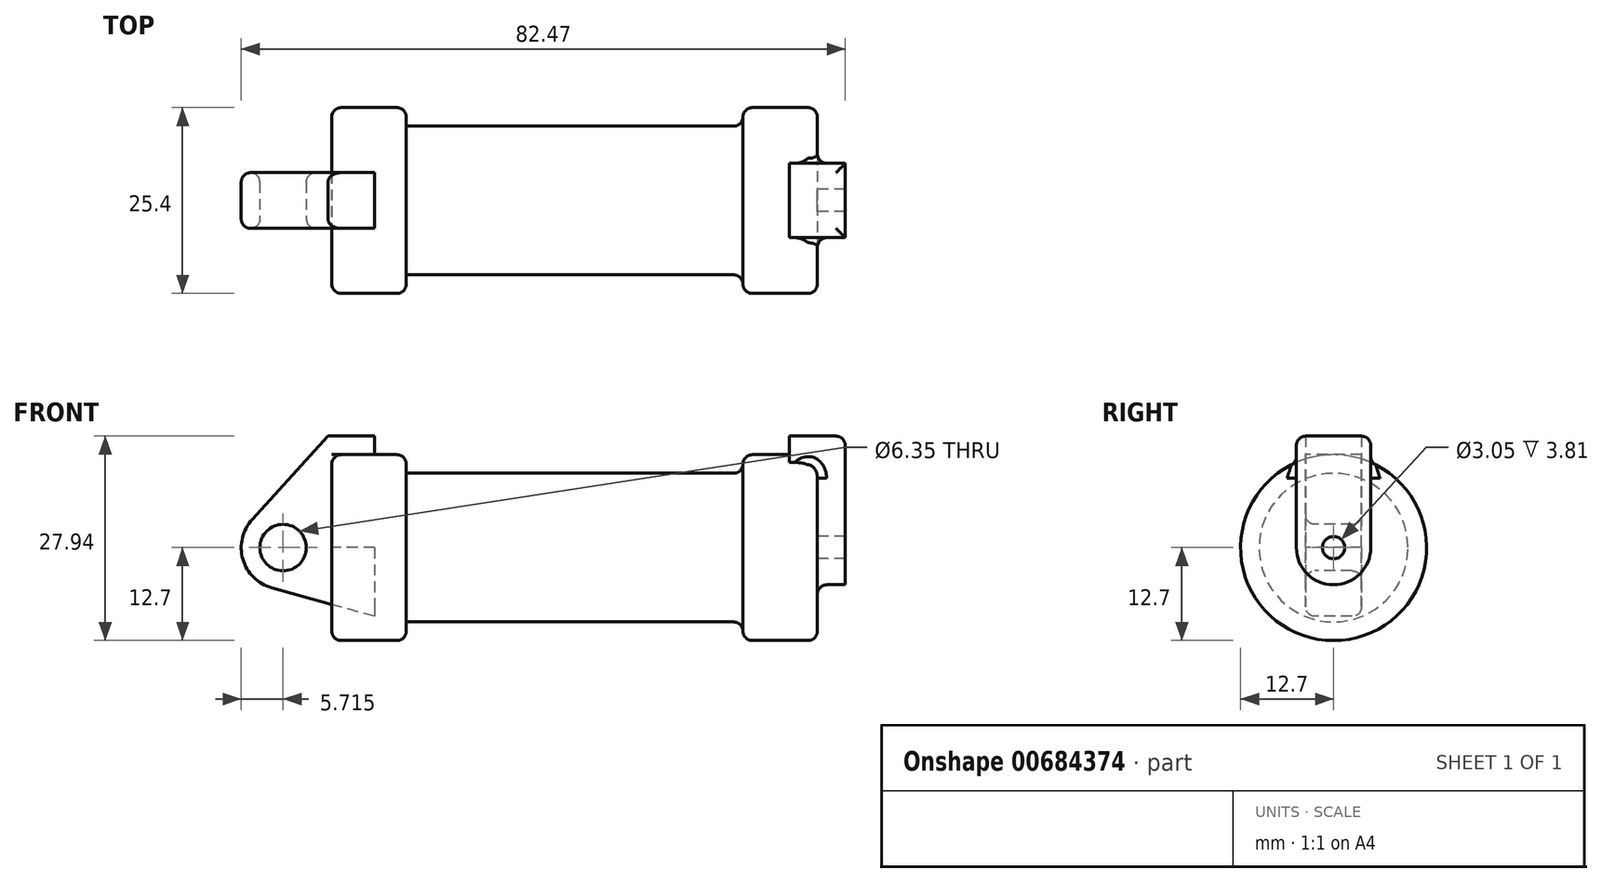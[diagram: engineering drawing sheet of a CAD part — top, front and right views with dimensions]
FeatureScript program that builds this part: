
annotation { "Feature Type Name" : "Feature", "Feature Type Description" : "" }
export const myFeature = defineFeature(function(context is Context, id is Id, definition is map)
    precondition{}
    {
        {
            var Q0;
            Q0=qCreatedBy(makeId("Front.planeOp"),FACE);
            var sketch = newSketch(context, id + "F0", { "sketchPlane" : qUnion([Q0])});
            skLineSegment(sketch, "E0", {"start": v(0, 0) * mm, "end": v(0, 12.7) * mm});
            skLineSegment(sketch, "E1", {"start": v(0, 12.7) * mm, "end": v(10.16, 12.7) * mm});
            skLineSegment(sketch, "E2", {"start": v(10.16, 12.7) * mm, "end": v(10.16, 10.16) * mm});
            skLineSegment(sketch, "E3", {"start": v(10.16, 10.16) * mm, "end": v(56.13, 10.16) * mm});
            skLineSegment(sketch, "E4", {"start": v(56.13, 10.16) * mm, "end": v(56.13, 12.7) * mm});
            skLineSegment(sketch, "E5", {"start": v(56.13, 12.7) * mm, "end": v(66.3, 12.7) * mm});
            skLineSegment(sketch, "E6", {"start": v(66.3, 12.7) * mm, "end": v(66.3, 0) * mm});
            skLineSegment(sketch, "E7", {"start": v(66.3, 0) * mm, "end": v(0, 0) * mm});
            skLineSegment(sketch, "E8", {"start": v(5.84, 15.24) * mm, "end": v(-0.5, 15.24) * mm});
            skLineSegment(sketch, "E9", {"start": v(-0.5, 15.24) * mm, "end": v(-10.88, 3.85) * mm});
            skLineSegment(sketch, "E10", {"start": v(0, 0) * mm, "end": v(-6.65, 0) * mm});
            skCircle(sketch, "E11", {"center": v(-6.65, 0) * mm, "radius": 5.72 * mm});
            skCircle(sketch, "E12", {"center": v(-6.65, 0) * mm, "radius": 3.18 * mm});
            skLineSegment(sketch, "E13", {"start": v(5.84, 15.24) * mm, "end": v(5.84, -9.4) * mm});
            skLineSegment(sketch, "E14", {"start": v(5.84, -9.4) * mm, "end": v(-8.18, -5.5) * mm});
            skSolve(sketch);
        }
        {
            var Q0;
            {var subQ0=sQuery(id+"F0.wireOp",EDGE,"E0");Q0=makeQuery(id+"F0.imprint","IMPRINT",FACE,{"disambiguationData":[TD([[makeQuery(id+"F0.imprint","IMPRINT",EDGE,{"derivedFrom":subQ0}),-1.0]])]});}
            var Q1;
            {var subQ0=sQuery(id+"F0.wireOp",EDGE,"E2");Q1=makeQuery(id+"F0.imprint","IMPRINT",FACE,{"disambiguationData":[TD([[makeQuery(id+"F0.imprint","IMPRINT",EDGE,{"derivedFrom":subQ0}),-1.0]])]});}
            var Q2;
            Q2=sQuery(id+"F0.wireOp",EDGE,"E7");
            var Q3;
            Q3=sQuery(id+"F0.wireOp",EDGE,"E7");
            revolve(context, id + "F1", {"entities" : qUnion([Q0, Q1]), "surfaceEntities" : qUnion([Q2]), "axis" : qUnion([Q3]), "revolveType" : RevolveType.FULL});
        }
        {
            var Q0;
            Q0=makeQuery(id+"F1.opRevolve","SWEPT_FACE",FACE,{"disambiguationData":[OSD([sQuery(id+"F0.wireOp",EDGE,"E6")])]});
            var sketch = newSketch(context, id + "F2", { "sketchPlane" : qUnion([Q0])});
            skCircle(sketch, "E15", {"center": v(0, 0) * mm, "radius": 5.08 * mm});
            skCircle(sketch, "E16", {"center": v(0, 0) * mm, "radius": 1.52 * mm});
            skPoint(sketch, "E17.start.orphan", {"position": v(12.7, 0) * mm});
            skLineSegment(sketch, "E18", {"start": v(-5.08, 0) * mm, "end": v(-5.08, 15.24) * mm});
            skLineSegment(sketch, "E19", {"start": v(5.08, 0) * mm, "end": v(5.08, 15.24) * mm});
            skLineSegment(sketch, "E20", {"start": v(-5.08, 15.24) * mm, "end": v(5.08, 15.24) * mm});
            skSolve(sketch);
        }
        {
            var Q0;
            {var subQ0=sQuery(id+"F0.wireOp",EDGE,"E14");Q0=makeQuery(id+"F0.imprint","IMPRINT",FACE,{"disambiguationData":[TD([[makeQuery(id+"F0.imprint","IMPRINT",EDGE,{"derivedFrom":subQ0}),-1.0]])]});}
            var Q1;
            {var subQ5=sQuery(id+"F0.wireOp",EDGE,"E12");Q1=makeQuery(id+"F0.imprint","IMPRINT",FACE,{"disambiguationData":[TD([[makeQuery(id+"F0.imprint","IMPRINT",EDGE,{"derivedFrom":subQ5}),-1.0]])]});}
            var Q2;
            {var subQ1=sQuery(id+"F0.wireOp",EDGE,"E0");Q2=makeQuery(id+"F0.imprint","IMPRINT",FACE,{"disambiguationData":[TD([[makeQuery(id+"F0.imprint","IMPRINT",EDGE,{"derivedFrom":subQ1}),1.0]])]});}
            extrude(context, id + "F3", {"entities" : qUnion([Q0, Q1, Q2]), "endBound" : BoundingType.SYMMETRIC, "oppositeDirection" : true, "depth" : 7.62 * mm, "offsetDistance" : 25.4 * mm});
        }
        {
            var Q0;
            Q0=qSketchRegion(id+"F2",true);
            extrude(context, id + "F4", {"entities" : qUnion([Q0]), "operationType" : NewBodyOperationType.ADD, "endBound" : BoundingType.SYMMETRIC, "depth" : 7.62 * mm, "offsetDistance" : 25.4 * mm});
        }
        {
            var Q0;
            Q0=makeQuery(id+"F4.boolean.opBoolean","SPLIT",FACE,{"disambiguationData":[TD([makeQuery(id+"F1.opRevolve","SWEPT_FACE",FACE,{"disambiguationData":[OSD([sQuery(id+"F0.wireOp",EDGE,"E5")])]})])],"derivedFrom":makeQuery(id+"F1.opRevolve","SWEPT_FACE",FACE,{"disambiguationData":[OSD([sQuery(id+"F0.wireOp",EDGE,"E6")])]})});
            var Q1;
            Q1=makeQuery(id+"F1.opRevolve","SWEPT_EDGE",EDGE,{"disambiguationData":[OSD([sQuery(id+"F0.wireOp",EDGE,"E3"),sQuery(id+"F0.wireOp",EDGE,"E4")])]});
            var Q2;
            Q2=makeQuery(id+"F1.opRevolve","SWEPT_EDGE",EDGE,{"disambiguationData":[OSD([sQuery(id+"F0.wireOp",EDGE,"E4"),sQuery(id+"F0.wireOp",EDGE,"E5")])]});
            var Q3;
            Q3=makeQuery(id+"F1.opRevolve","SWEPT_EDGE",EDGE,{"disambiguationData":[OSD([sQuery(id+"F0.wireOp",EDGE,"E1"),sQuery(id+"F0.wireOp",EDGE,"E2")])]});
            var Q4;
            Q4=makeQuery(id+"F1.opRevolve","SWEPT_EDGE",EDGE,{"disambiguationData":[OSD([sQuery(id+"F0.wireOp",EDGE,"E0"),sQuery(id+"F0.wireOp",EDGE,"E1")])]});
            var Q5;
            Q5=makeQuery(id+"F3.opExtrude","CAP_EDGE",EDGE,{"disambiguationData":[OSD([sQuery(id+"F0.wireOp",EDGE,"E12")])],"isStart":false});
            var Q6;
            Q6=makeQuery(id+"F3.opExtrude","CAP_EDGE",EDGE,{"disambiguationData":[OSD([sQuery(id+"F0.wireOp",EDGE,"E12")])],"isStart":true});
            var Q7;
            Q7=makeQuery(id+"F3.opExtrude","CAP_EDGE",EDGE,{"disambiguationData":[OSD([sQuery(id+"F0.wireOp",EDGE,"E9")])],"isStart":true});
            var Q8;
            Q8=makeQuery(id+"F3.opExtrude","CAP_EDGE",EDGE,{"disambiguationData":[OSD([sQuery(id+"F0.wireOp",EDGE,"E9")])],"isStart":false});
            var Q9;
            Q9=makeQuery(id+"F4.opExtrude","CAP_EDGE",EDGE,{"disambiguationData":[OSD([sQuery(id+"F2.wireOp",EDGE,"E20")])],"isStart":false});
            var Q10;
            Q10=makeQuery(id+"F4.opExtrude","SWEPT_EDGE",EDGE,{"disambiguationData":[OSD([sQuery(id+"F2.wireOp",EDGE,"E19"),sQuery(id+"F2.wireOp",EDGE,"E20")])]});
            var Q11;
            Q11=makeQuery(id+"F4.opExtrude","SWEPT_EDGE",EDGE,{"disambiguationData":[OSD([sQuery(id+"F2.wireOp",EDGE,"E18"),sQuery(id+"F2.wireOp",EDGE,"E20")])]});
            var Q12;
            Q12=makeQuery(id+"F4.boolean.opBoolean","INTERSECT",EDGE,{"derivedFrom":[makeQuery(id+"F1.opRevolve","SWEPT_FACE",FACE,{"disambiguationData":[OSD([sQuery(id+"F0.wireOp",EDGE,"E6")])]}),makeQuery(id+"F4.opExtrude","SWEPT_FACE",FACE,{"disambiguationData":[OSD([sQuery(id+"F2.wireOp",EDGE,"E18")])]})]});
            fillet(context, id + "F5", {"entities" : qUnion([Q0, Q1, Q2, Q3, Q4, Q5, Q6, Q7, Q8, Q9, Q10, Q11, Q12]), "radius" : 1.27 * mm, "tangentPropagation" : true, "allowEdgeOverflow" : false});
        }
    });
